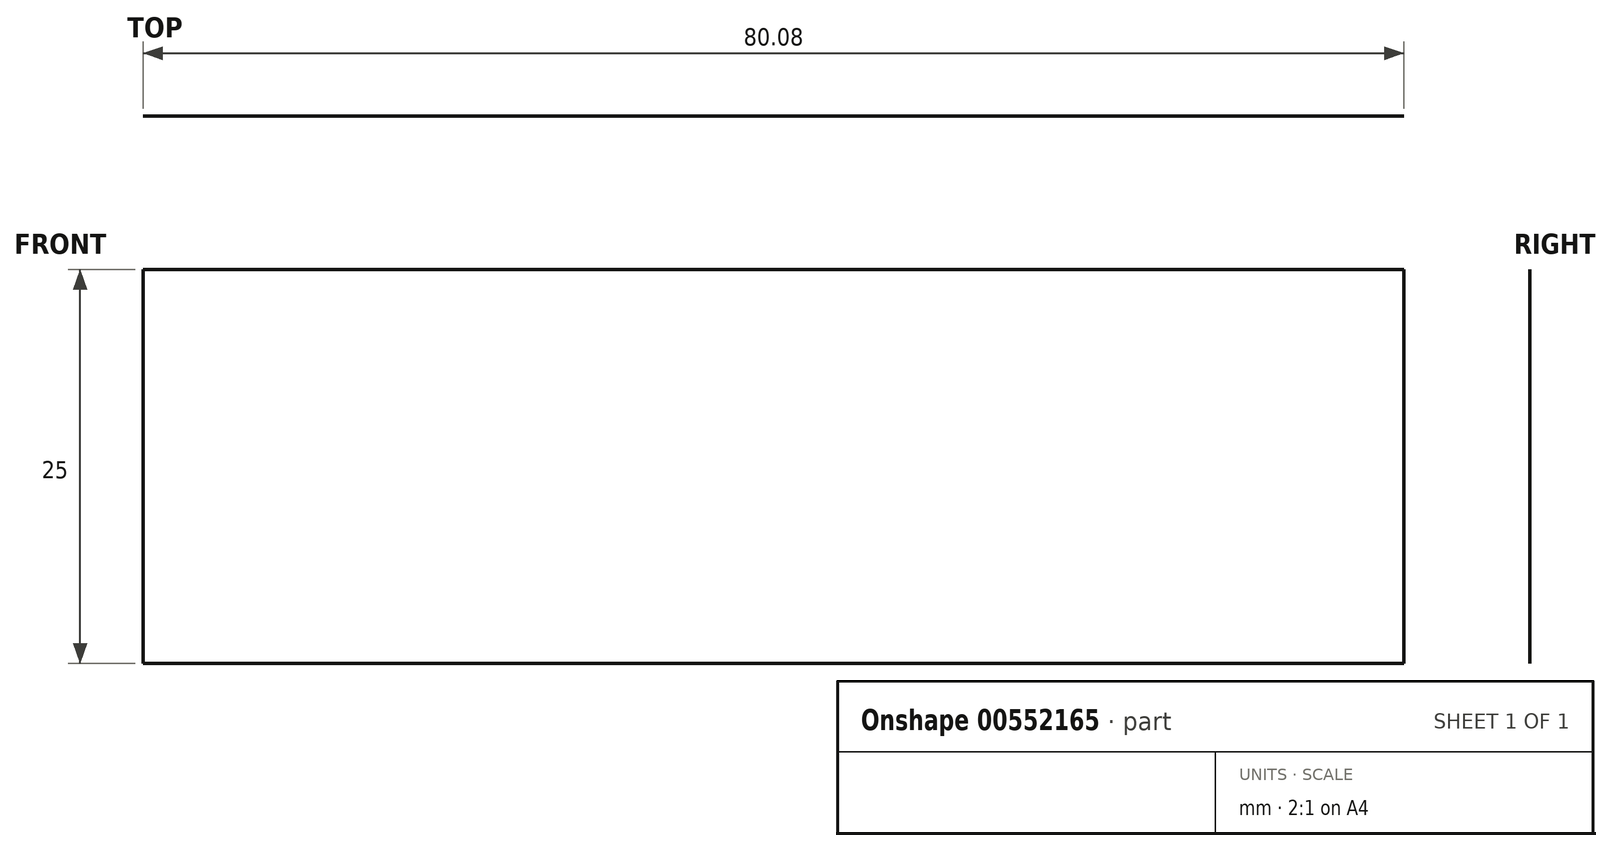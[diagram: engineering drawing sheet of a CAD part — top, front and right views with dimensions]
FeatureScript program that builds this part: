
annotation { "Feature Type Name" : "Feature", "Feature Type Description" : "" }
export const myFeature = defineFeature(function(context is Context, id is Id, definition is map)
    precondition{}
    {
        {
            var Q0;
            Q0=qCreatedBy(makeId("Top.planeOp"),FACE);
            var sketch = newSketch(context, id + "F0", { "sketchPlane" : qUnion([Q0])});
            skLineSegment(sketch, "E0", {"start": v(-38.12, 17.36) * mm, "end": v(41.96, 17.36) * mm});
            skSolve(sketch);
        }
        {
            var Q0;
            Q0=sQuery(id+"F0.wireOp",EDGE,"E0");
            extrude(context, id + "F1", {"bodyType" : ToolBodyType.SURFACE, "surfaceEntities" : qUnion([Q0]), "depth" : 25 * mm, "offsetDistance" : 25 * mm});
        }
    });
